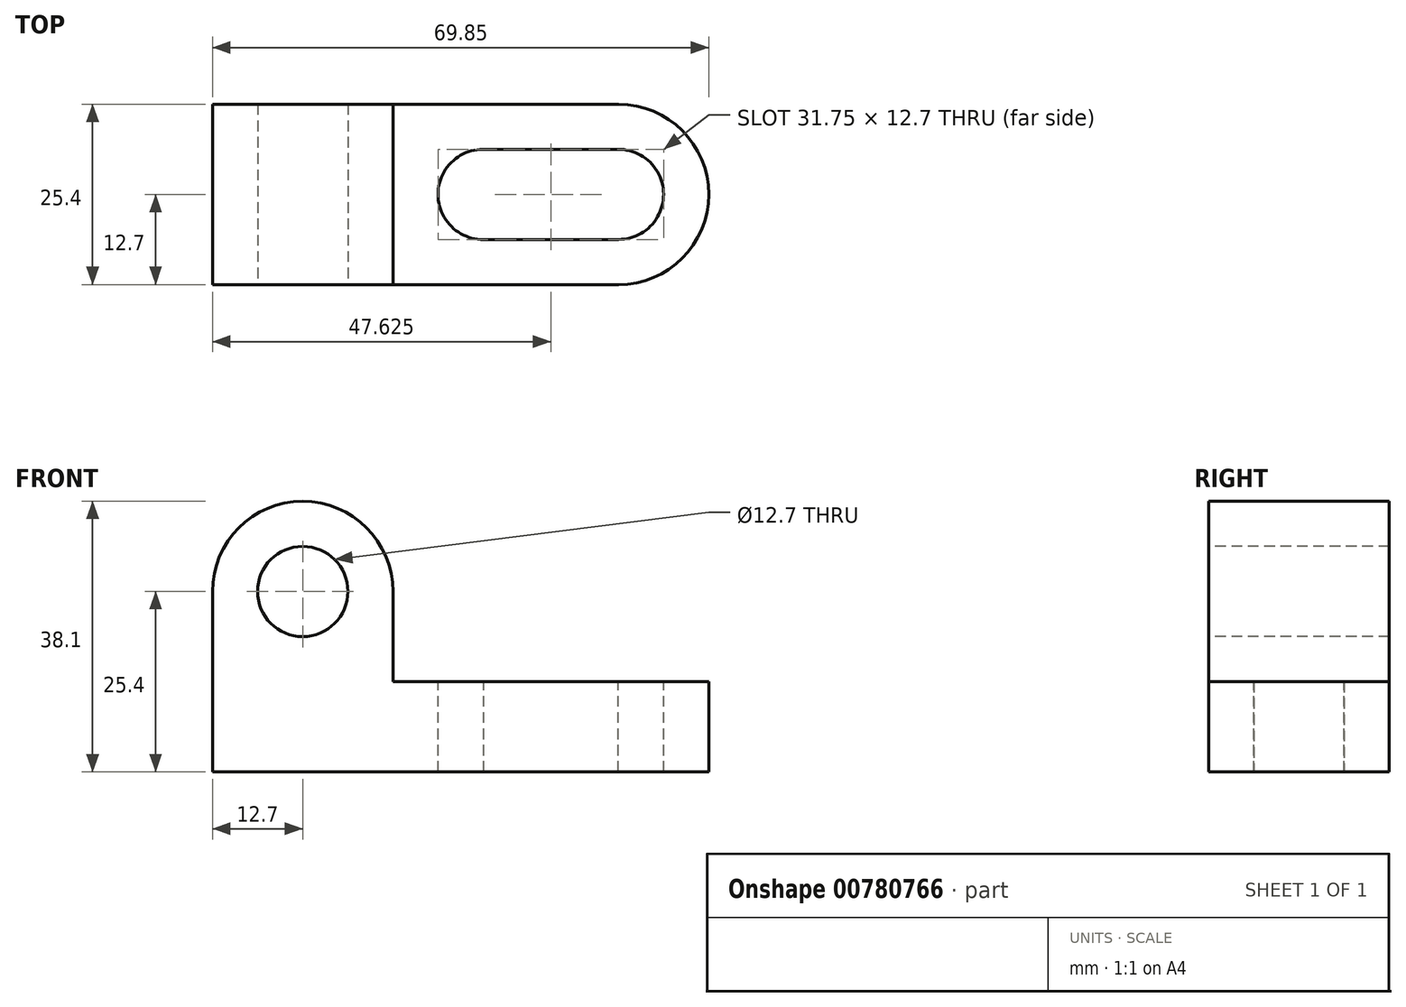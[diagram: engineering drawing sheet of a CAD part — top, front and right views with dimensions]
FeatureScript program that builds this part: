
annotation { "Feature Type Name" : "Feature", "Feature Type Description" : "" }
export const myFeature = defineFeature(function(context is Context, id is Id, definition is map)
    precondition{}
    {
        {
            var Q0;
            Q0=qCreatedBy(makeId("Front.planeOp"),FACE);
            var sketch = newSketch(context, id + "F0", { "sketchPlane" : qUnion([Q0])});
            skLineSegment(sketch, "E0", {"start": v(0, 0) * mm, "end": v(69.85, 0) * mm});
            skLineSegment(sketch, "E1", {"start": v(69.85, 0) * mm, "end": v(69.85, 12.7) * mm});
            skLineSegment(sketch, "E2", {"start": v(69.85, 12.7) * mm, "end": v(25.4, 12.7) * mm});
            skLineSegment(sketch, "E3", {"start": v(25.4, 12.7) * mm, "end": v(25.4, 38.1) * mm});
            skLineSegment(sketch, "E4", {"start": v(25.4, 38.1) * mm, "end": v(0, 38.1) * mm});
            skLineSegment(sketch, "E5", {"start": v(0, 38.1) * mm, "end": v(0, 0) * mm});
            skSolve(sketch);
        }
        {
            var Q0;
            Q0 = qSketchRegion(id + "F0", true);
            extrude(context, id + "F1", {"entities" : qUnion([Q0]), "depth" : 25.4 * mm, "offsetDistance" : 25.4 * mm});
        }
        {
            var Q0;
            Q0=makeQuery(id+"F1.opExtrude","CAP_EDGE",EDGE,{"disambiguationData":[OSD([sQuery(id+"F0.wireOp",EDGE,"E1")])],"isStart":false});
            var Q1;
            Q1=makeQuery(id+"F1.opExtrude","CAP_EDGE",EDGE,{"disambiguationData":[OSD([sQuery(id+"F0.wireOp",EDGE,"E1")])],"isStart":true});
            var Q2;
            Q2=makeQuery(id+"F1.opExtrude","SWEPT_EDGE",EDGE,{"disambiguationData":[OSD([sQuery(id+"F0.wireOp",EDGE,"E3"),sQuery(id+"F0.wireOp",EDGE,"E4")])]});
            var Q3;
            Q3=makeQuery(id+"F1.opExtrude","SWEPT_EDGE",EDGE,{"disambiguationData":[OSD([sQuery(id+"F0.wireOp",EDGE,"E4"),sQuery(id+"F0.wireOp",EDGE,"E5")])]});
            fillet(context, id + "F2", {"entities" : qUnion([Q0, Q1, Q2, Q3]), "radius" : 12.7 * mm, "tangentPropagation" : true, "allowEdgeOverflow" : false});
        }
        {
            var Q0;
            Q0=makeQuery(id+"F1.opExtrude","CAP_FACE",FACE,{"disambiguationData":[OSD([sQuery(id+"F0.wireOp",EDGE,"E0"),sQuery(id+"F0.wireOp",EDGE,"E1"),sQuery(id+"F0.wireOp",EDGE,"E2"),sQuery(id+"F0.wireOp",EDGE,"E3"),sQuery(id+"F0.wireOp",EDGE,"E4"),sQuery(id+"F0.wireOp",EDGE,"E5")])],"isStart":false});
            var sketch = newSketch(context, id + "F3", { "sketchPlane" : qUnion([Q0])});
            skCircle(sketch, "E6", {"center": v(12.7, 25.4) * mm, "radius": 6.35 * mm});
            skSolve(sketch);
        }
        {
            var Q0;
            Q0=makeQuery(id+"F3.imprint","IMPRINT",FACE,{"disambiguationData":[TD([[makeQuery(id+"F3.imprint","IMPRINT",EDGE,{"derivedFrom":sQuery(id+"F3.wireOp",EDGE,"E6")}),1.0]])]});
            extrude(context, id + "F4", {"entities" : qUnion([Q0]), "operationType" : NewBodyOperationType.REMOVE, "oppositeDirection" : true, "depth" : 25.4 * mm, "offsetDistance" : 25.4 * mm});
        }
        {
            var Q0;
            Q0=makeQuery(id+"F1.opExtrude","SWEPT_FACE",FACE,{"disambiguationData":[OSD([sQuery(id+"F0.wireOp",EDGE,"E2")])]});
            var sketch = newSketch(context, id + "F5", { "sketchPlane" : qUnion([Q0])});
            skCircle(sketch, "E7", {"center": v(38.1, -12.7) * mm, "radius": 6.35 * mm});
            skCircle(sketch, "E8", {"center": v(57.15, -12.7) * mm, "radius": 6.35 * mm});
            skLineSegment(sketch, "E9", {"start": v(38.17, -19.05) * mm, "end": v(57.15, -19.05) * mm});
            skLineSegment(sketch, "E10", {"start": v(38.1, -6.35) * mm, "end": v(57.15, -6.35) * mm});
            skSolve(sketch);
        }
        {
            var Q0;
            Q0 = qSketchRegion(id + "F5", true);
            extrude(context, id + "F6", {"entities" : qUnion([Q0]), "operationType" : NewBodyOperationType.REMOVE, "oppositeDirection" : true, "depth" : 25.4 * mm, "offsetDistance" : 25.4 * mm});
        }
    });
